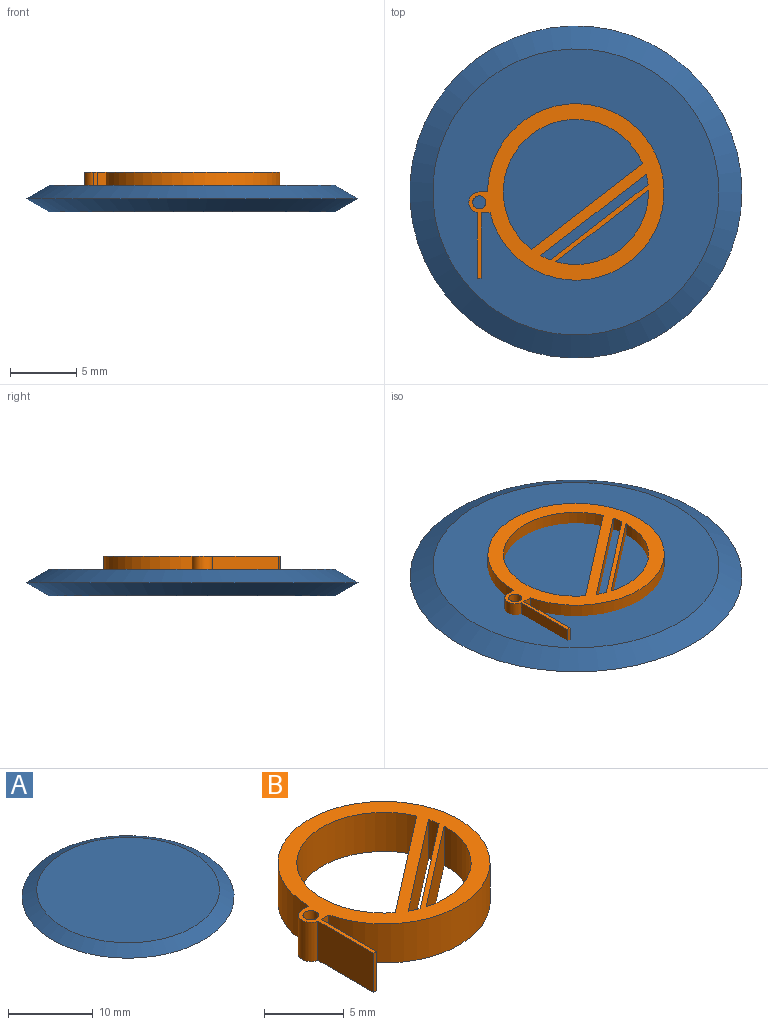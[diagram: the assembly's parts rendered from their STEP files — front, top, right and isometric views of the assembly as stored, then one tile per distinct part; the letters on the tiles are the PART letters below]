
ASSEMBLY  parts=2 mates=1
PART A: 4 faces, bbox 25x25x2 mm
  f0: plane 21.54x21.54mm, normal (0,0,1), area 364.3mm2, adj f1
  f1: cone r=12.5mm half-angle=60deg, axis (0,0,-1), area 146.2mm2, adj f0,f2
  f2: cone r=12.5mm half-angle=60deg, axis (0,0,1), area 146.2mm2, adj f1,f3
  f3: plane 21.54x21.54mm, normal (0,0,-1), area 364.3mm2, adj f2
PART B: 18 faces, bbox 14.7x13.3x3 mm
  f0: cylinder r=6.64mm len=13.29mm, axis (0,0,-1), area 120.5mm2, adj f1,f11,f16,f17
  f1: plane 3x0.68mm, normal (0,-1,0), area 2mm2, adj f0,f2,f16,f17
  f2: plane 4.93x3mm, normal (1,0,0), area 14.8mm2, adj f1,f3,f16,f17
  f3: plane 3x0.28mm, normal (0,-1,0), area 0.8mm2, adj f2,f4,f16,f17
  f4: plane 4.95x3mm, normal (-1,0,0), area 14.8mm2, adj f3,f5,f16,f17
  f5: cylinder r=0.79mm len=3mm, axis (0,0,-1), area 7mm2, adj f4,f11,f16,f17
  f6: plane 8.36x6.46mm, normal (-0.61,0.79,0), area 31.7mm2, adj f12,f16,f17
  f7: plane 7.34x5.67mm, normal (-0.61,0.79,0), area 27.8mm2, adj f8,f13,f16,f17
  f8: cylinder r=5.46mm len=3mm, axis (0,0,-1), area 2.4mm2, adj f7,f9,f16,f17
  f9: plane 7.93x6.13mm, normal (0.61,-0.79,0), area 30.1mm2, adj f8,f13,f16,f17
  f10: cylinder r=5.46mm len=6.98mm, axis (0,0,-1), area 30.8mm2, adj f14,f16,f17
  f11: plane 3x0.62mm, normal (0,1,0), area 1.9mm2, adj f0,f5,f16,f17
  f12: cylinder r=5.46mm len=10.49mm, axis (0,0,-1), area 59.9mm2, adj f6,f16,f17
  f13: cylinder r=5.46mm len=3mm, axis (0,0,-1), area 2.4mm2, adj f7,f9,f16,f17
  f14: plane 6.97x5.39mm, normal (0.61,-0.79,0), area 26.4mm2, adj f10,f16,f17
  f15: cylinder r=0.49mm len=3mm, axis (0,0,-1), area 9.2mm2, adj f16,f17
  f16: plane 14.7x13.29mm, normal (0,0,1), area 58.8mm2, adj f0,f1,f2,f3,f4,f5,f6,f7
  f17: plane 14.7x13.29mm, normal (0,0,-1), area 58.8mm2, adj f0,f1,f2,f3,f4,f5,f6,f7
PLACE A t=(-90.02,-0.12,-1.05)mm
PLACE B t=(-90.02,-0.12,-1.05)mm
MATE fastened A.f1 <-> B.f0  axis (0,0,1) through (-0.02,-0.12,-0.05)mm
